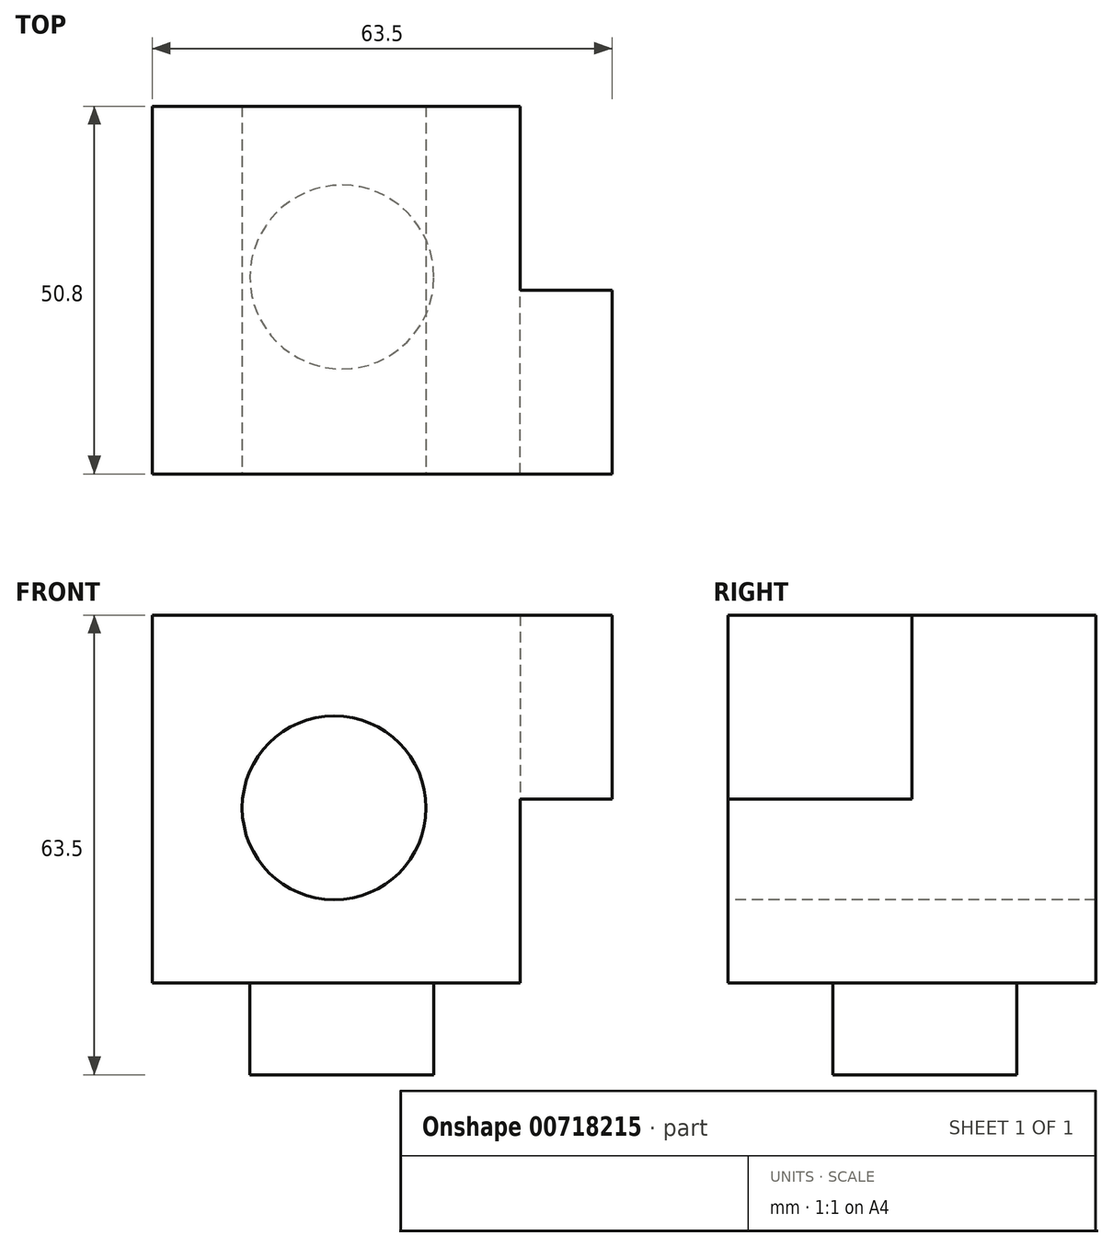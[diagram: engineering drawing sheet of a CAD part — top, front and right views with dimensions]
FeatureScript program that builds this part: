
annotation { "Feature Type Name" : "Feature", "Feature Type Description" : "" }
export const myFeature = defineFeature(function(context is Context, id is Id, definition is map)
    precondition{}
    {
        {
            var Q0;
            Q0=qCreatedBy(makeId("Front.planeOp"),FACE);
            var sketch = newSketch(context, id + "F0", { "sketchPlane" : qUnion([Q0])});
            skLineSegment(sketch, "E0", {"start": v(0, 0) * mm, "end": v(0, 50.8) * mm});
            skLineSegment(sketch, "E1", {"start": v(0, 50.8) * mm, "end": v(50.8, 50.8) * mm});
            skLineSegment(sketch, "E2", {"start": v(50.8, 50.8) * mm, "end": v(50.8, 0) * mm});
            skLineSegment(sketch, "E3", {"start": v(50.8, 0) * mm, "end": v(0, 0) * mm});
            skSolve(sketch);
        }
        {
            var Q0;
            Q0 = qSketchRegion(id + "F0", true);
            var Q1;
            Q1=makeQuery(id+"F0.imprint","IMPRINT",FACE,{"disambiguationData":[TD([[makeQuery(id+"F0.imprint","IMPRINT",EDGE,{"derivedFrom":sQuery(id+"F0.wireOp",EDGE,"E0")}),-1.0]])]});
            extrude(context, id + "F1", {"entities" : qUnion([Q0, Q1]), "depth" : 50.8 * mm, "offsetDistance" : 25.4 * mm});
        }
        {
            var Q0;
            Q0=makeQuery(id+"F1.opExtrude","CAP_FACE",FACE,{"disambiguationData":[OSD([sQuery(id+"F0.wireOp",EDGE,"E0"),sQuery(id+"F0.wireOp",EDGE,"E1"),sQuery(id+"F0.wireOp",EDGE,"E2"),sQuery(id+"F0.wireOp",EDGE,"E3")])],"isStart":false});
            var sketch = newSketch(context, id + "F2", { "sketchPlane" : qUnion([Q0])});
            skCircle(sketch, "E4", {"center": v(25.11, 24.16) * mm, "radius": 12.7 * mm});
            skSolve(sketch);
        }
        {
            var Q0;
            Q0=makeQuery(id+"F2.imprint","IMPRINT",FACE,{"disambiguationData":[TD([[makeQuery(id+"F2.imprint","IMPRINT",EDGE,{"derivedFrom":sQuery(id+"F2.wireOp",EDGE,"E4")}),1.0]])]});
            extrude(context, id + "F3", {"entities" : qUnion([Q0]), "operationType" : NewBodyOperationType.REMOVE, "oppositeDirection" : true, "depth" : 50.8 * mm, "offsetDistance" : 25.4 * mm});
        }
        {
            var Q0;
            Q0=makeQuery(id+"F1.opExtrude","SWEPT_FACE",FACE,{"disambiguationData":[OSD([sQuery(id+"F0.wireOp",EDGE,"E3")])]});
            var sketch = newSketch(context, id + "F4", { "sketchPlane" : qUnion([Q0])});
            skCircle(sketch, "E5", {"center": v(26.19, 23.62) * mm, "radius": 12.7 * mm});
            skSolve(sketch);
        }
        {
            var Q0;
            Q0 = qSketchRegion(id + "F4", true);
            extrude(context, id + "F5", {"entities" : qUnion([Q0]), "operationType" : NewBodyOperationType.ADD, "depth" : 12.7 * mm, "offsetDistance" : 25.4 * mm});
        }
        {
            var Q0;
            Q0=makeQuery(id+"F1.opExtrude","SWEPT_FACE",FACE,{"disambiguationData":[OSD([sQuery(id+"F0.wireOp",EDGE,"E2")])]});
            var sketch = newSketch(context, id + "F6", { "sketchPlane" : qUnion([Q0])});
            skLineSegment(sketch, "E6.bottom", {"start": v(-50.8, 50.8) * mm, "end": v(-25.4, 50.8) * mm});
            skLineSegment(sketch, "E6.top", {"start": v(-50.8, 25.4) * mm, "end": v(-25.4, 25.4) * mm});
            skLineSegment(sketch, "E6.left", {"start": v(-50.8, 50.8) * mm, "end": v(-50.8, 25.4) * mm});
            skLineSegment(sketch, "E6.right", {"start": v(-25.4, 50.8) * mm, "end": v(-25.4, 25.4) * mm});
            skSolve(sketch);
        }
        {
            var Q0;
            Q0 = qSketchRegion(id + "F6", true);
            extrude(context, id + "F7", {"entities" : qUnion([Q0]), "operationType" : NewBodyOperationType.ADD, "depth" : 12.7 * mm, "offsetDistance" : 25.4 * mm});
        }
    });
